# Revit family: Gira_201400
name_source: partatom
category: Electrical Fixtures
revit_build: Autodesk Revit 2017 (Build: 20160225_1515(x64)
units: mm (PartAtom-declared; Revit-internal decimal feet)

## family parameters
Cut with Voids When Loaded = No
Host = Face
Maintain Annotation Orientation = No
Part Type = Normal
Room Calculation Point = No
Round Connector Dimension = Use Diameter
Shared = No

## types (1)
- USB data I/F DRA KNX DRA
    BIM = https://media.live.bim.site X1 REG KNX.rfa
    BIMSITE_PRODUCT_ID = 04f23a842058d81640a22a3f83dca06389e7449b
    Bus connection included = Yes
    Colour = Sonstige (*de-DE)
    Cost = 0 $
    Default Elevation = 1219 mm
    GTIN = 4010337072928
    HAN = 201400
    HeinzeBIM = https://www.heinze.de
    Manufacturer = Gira
    Material = plastic
    Material quality = Thermoplastic
    Model = USB
    Radio frequent bidirectional = No
    Surface finishing = Not applicable
    Surface protection = Sonstige (*de-DE)
    Transparent = No
    URL = https://www.gira.de
    With label area = Yes

## geometry (parser evidence)
native form markers: Blend x2, Sweep x3
no freeform markers — native parametric forms only
